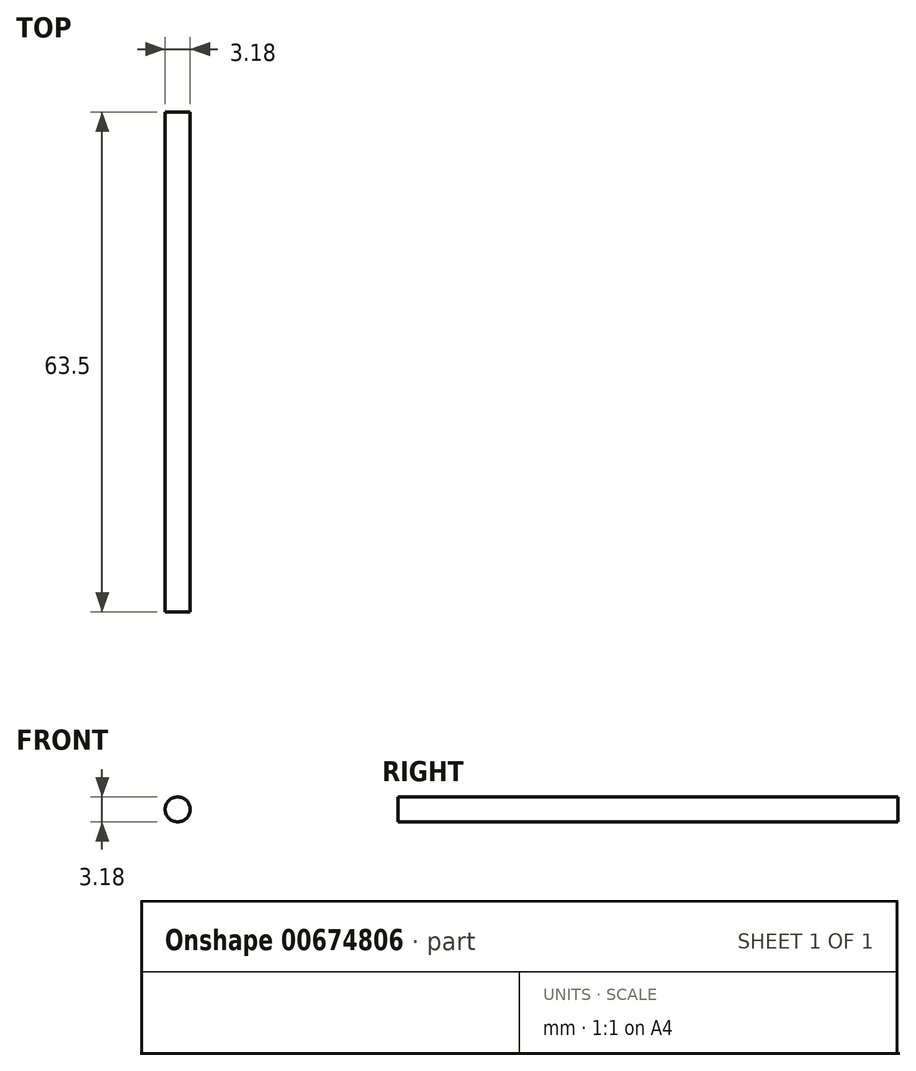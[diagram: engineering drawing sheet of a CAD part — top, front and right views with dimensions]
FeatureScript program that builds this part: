
annotation { "Feature Type Name" : "Feature", "Feature Type Description" : "" }
export const myFeature = defineFeature(function(context is Context, id is Id, definition is map)
    precondition{}
    {
        {
            var Q0;
            Q0=qCreatedBy(makeId("Front.planeOp"),FACE);
            var sketch = newSketch(context, id + "F0", { "sketchPlane" : qUnion([Q0])});
            skCircle(sketch, "E0", {"center": v(0, 0) * mm, "radius": 1.59 * mm});
            skSolve(sketch);
        }
        {
            var Q0;
            Q0 = qSketchRegion(id + "F0", true);
            extrude(context, id + "F1", {"entities" : qUnion([Q0]), "oppositeDirection" : true, "depth" : 63.5 * mm, "offsetDistance" : 25.4 * mm});
        }
    });
